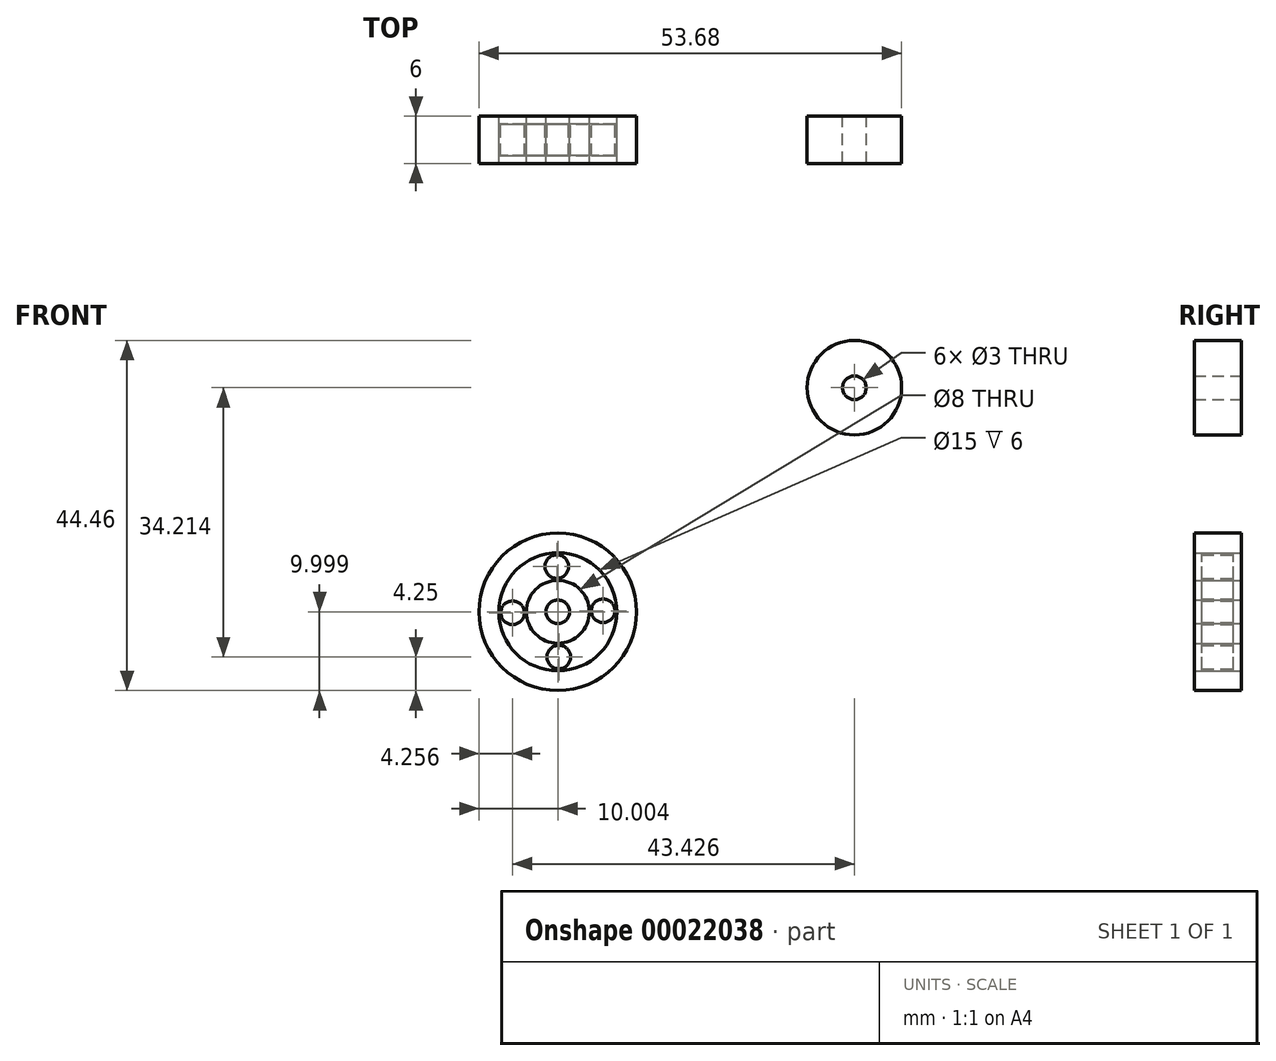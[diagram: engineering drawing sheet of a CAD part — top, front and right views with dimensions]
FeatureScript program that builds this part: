
annotation { "Feature Type Name" : "Feature", "Feature Type Description" : "" }
export const myFeature = defineFeature(function(context is Context, id is Id, definition is map)
    precondition{}
    {
        {
            var Q0;
            Q0=qCreatedBy(makeId("Front.planeOp"),FACE);
            var sketch = newSketch(context, id + "F0", { "sketchPlane" : qUnion([Q0])});
            skCircle(sketch, "E0", {"center": v(-14.69, -14.78) * mm, "radius": 10 * mm});
            skCircle(sketch, "E1", {"center": v(-14.69, -14.78) * mm, "radius": 4 * mm});
            skCircle(sketch, "E2", {"center": v(-14.69, -14.78) * mm, "radius": 1.5 * mm});
            skCircle(sketch, "E3", {"center": v(-14.69, -14.78) * mm, "radius": 7.5 * mm});
            skCircle(sketch, "E4", {"center": v(-14.56, -20.53) * mm, "radius": 1.5 * mm});
            skCircle(sketch, "E5.1.0", {"center": v(-8.94, -14.65) * mm, "radius": 1.5 * mm});
            skCircle(sketch, "E5.2.0", {"center": v(-14.81, -9.03) * mm, "radius": 1.5 * mm});
            skCircle(sketch, "E5.3.0", {"center": v(-20.43, -14.9) * mm, "radius": 1.5 * mm});
            skSolve(sketch);
        }
        {
            var Q0;
            Q0=makeQuery(id+"F0.imprint","IMPRINT",FACE,{"disambiguationData":[TD([[makeQuery(id+"F0.imprint","IMPRINT",EDGE,{"derivedFrom":sQuery(id+"F0.wireOp",EDGE,"E0")}),1.0]])]});
            var Q1;
            Q1=makeQuery(id+"F0.imprint","IMPRINT",FACE,{"disambiguationData":[TD([[makeQuery(id+"F0.imprint","IMPRINT",EDGE,{"derivedFrom":sQuery(id+"F0.wireOp",EDGE,"E1")}),1.0]])]});
            extrude(context, id + "F1", {"entities" : qUnion([Q0, Q1]), "endBound" : BoundingType.SYMMETRIC, "depth" : 6 * mm});
        }
        {
            var Q0;
            Q0=makeQuery(id+"F0.imprint","IMPRINT",FACE,{"disambiguationData":[TD([[makeQuery(id+"F0.imprint","IMPRINT",EDGE,{"derivedFrom":sQuery(id+"F0.wireOp",EDGE,"E3")}),1.0]])]});
            extrude(context, id + "F2", {"entities" : qUnion([Q0]), "endBound" : BoundingType.SYMMETRIC, "depth" : 4 * mm});
        }
        {
            var Q0;
            Q0=qCreatedBy(makeId("Front.planeOp"),FACE);
            var sketch = newSketch(context, id + "F3", { "sketchPlane" : qUnion([Q0])});
            skCircle(sketch, "E6", {"center": v(23, 13.68) * mm, "radius": 6 * mm});
            skCircle(sketch, "E7", {"center": v(23, 13.68) * mm, "radius": 1.5 * mm});
            skSolve(sketch);
        }
        {
            var Q0;
            Q0=makeQuery(id+"F3.imprint","IMPRINT",FACE,{"disambiguationData":[TD([[makeQuery(id+"F3.imprint","IMPRINT",EDGE,{"derivedFrom":sQuery(id+"F3.wireOp",EDGE,"E6")}),1.0]])]});
            extrude(context, id + "F4", {"entities" : qUnion([Q0]), "endBound" : BoundingType.SYMMETRIC, "depth" : 6 * mm});
        }
    });
